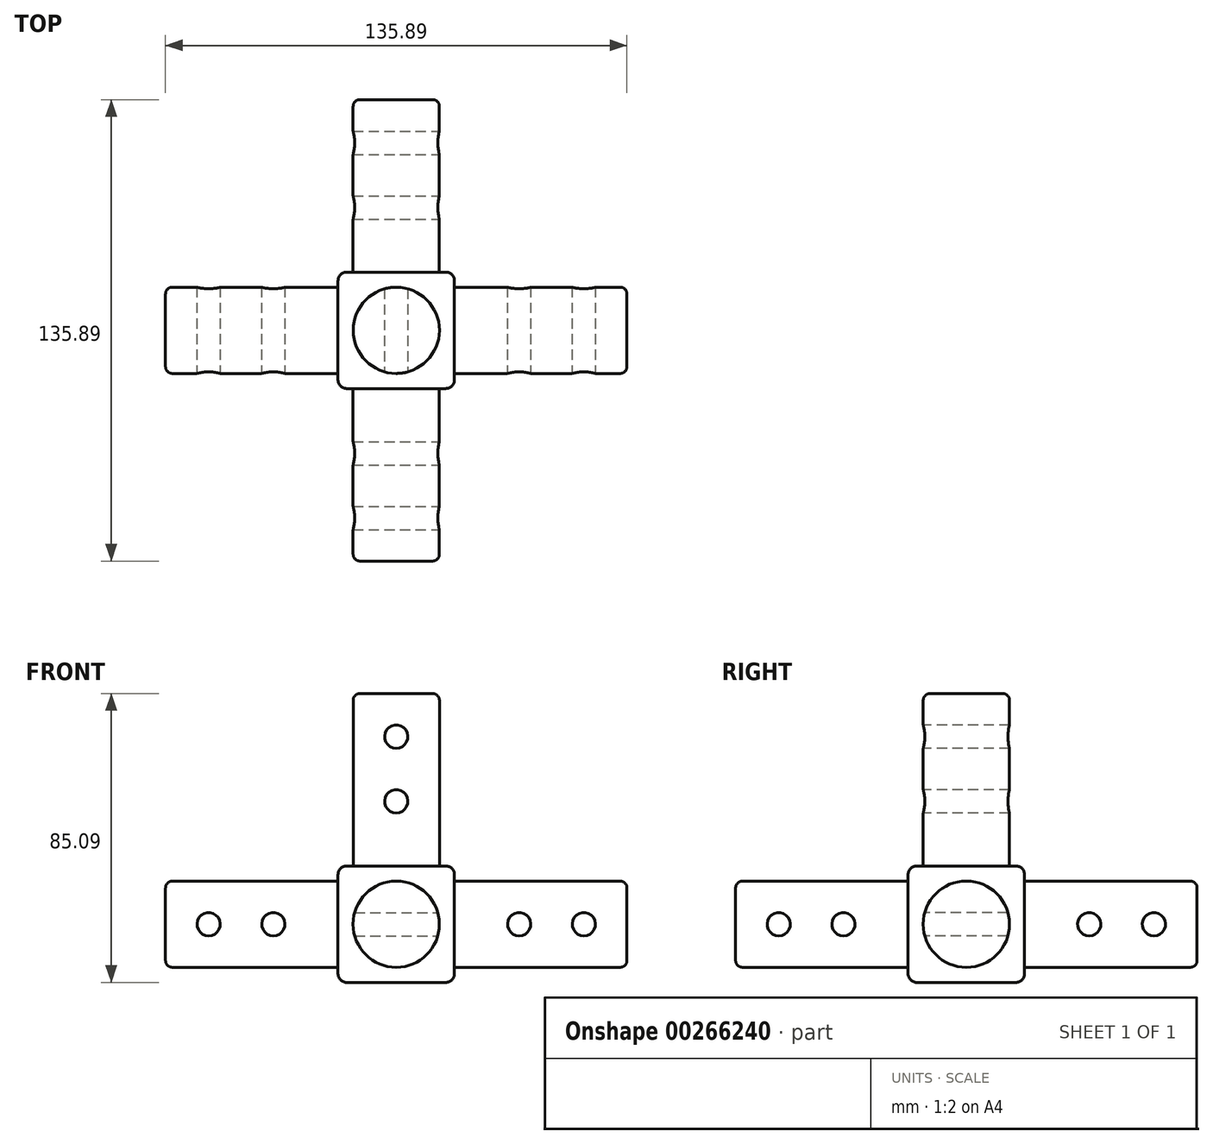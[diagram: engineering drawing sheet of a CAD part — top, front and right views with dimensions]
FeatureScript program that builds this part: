
annotation { "Feature Type Name" : "Feature", "Feature Type Description" : "" }
export const myFeature = defineFeature(function(context is Context, id is Id, definition is map)
    precondition{}
    {
        {
            var Q0;
            Q0=qCreatedBy(makeId("Top.planeOp"),FACE);
            var sketch = newSketch(context, id + "F0", { "sketchPlane" : qUnion([Q0])});
            skLineSegment(sketch, "E0.bottom", {"start": v(-13.47, 23.7) * mm, "end": v(20.82, 23.7) * mm});
            skLineSegment(sketch, "E0.top", {"start": v(-13.47, -10.58) * mm, "end": v(20.82, -10.58) * mm});
            skLineSegment(sketch, "E0.left", {"start": v(-13.47, 23.7) * mm, "end": v(-13.47, -10.58) * mm});
            skLineSegment(sketch, "E0.right", {"start": v(20.82, 23.7) * mm, "end": v(20.82, -10.58) * mm});
            skSolve(sketch);
        }
        {
            var Q0;
            Q0=qSketchRegion(id+"F0",true);
            extrude(context, id + "F1", {"entities" : qUnion([Q0]), "depth" : 34.3 * mm});
        }
        {
            var Q0;
            Q0=makeQuery(id+"F1.opExtrude","CAP_FACE",FACE,{"disambiguationData":[OSD([sQuery(id+"F0.wireOp",EDGE,"E0.bottom"),sQuery(id+"F0.wireOp",EDGE,"E0.top"),sQuery(id+"F0.wireOp",EDGE,"E0.left"),sQuery(id+"F0.wireOp",EDGE,"E0.right")])],"isStart":false});
            var sketch = newSketch(context, id + "F2", { "sketchPlane" : qUnion([Q0])});
            skCircle(sketch, "E1", {"center": v(3.68, 6.56) * mm, "radius": 12.7 * mm});
            skLineSegment(sketch, "E2", {"start": v(3.67, 23.7) * mm, "end": v(3.67, -12.79) * mm, "construction": true});
            skLineSegment(sketch, "E3", {"start": v(20.82, 6.56) * mm, "end": v(-13.47, 6.56) * mm, "construction": true});
            skSolve(sketch);
        }
        {
            var Q0;
            Q0=qSketchRegion(id+"F2",true);
            extrude(context, id + "F3", {"entities" : qUnion([Q0]), "operationType" : NewBodyOperationType.ADD, "depth" : 50.8 * mm});
        }
        {
            var Q0;
            Q0=makeQuery(id+"F1.opExtrude","SWEPT_FACE",FACE,{"disambiguationData":[OSD([sQuery(id+"F0.wireOp",EDGE,"E0.left")])]});
            var sketch = newSketch(context, id + "F4", { "sketchPlane" : qUnion([Q0])});
            skLineSegment(sketch, "E4", {"start": v(-23.7, 17.15) * mm, "end": v(13.45, 17.15) * mm, "construction": true});
            skLineSegment(sketch, "E5", {"start": v(-6.56, 0) * mm, "end": v(-6.56, 34.3) * mm, "construction": true});
            skCircle(sketch, "E6", {"center": v(-6.56, 17.15) * mm, "radius": 12.7 * mm});
            skSolve(sketch);
        }
        {
            var Q0;
            Q0=qSketchRegion(id+"F4",true);
            extrude(context, id + "F5", {"entities" : qUnion([Q0]), "operationType" : NewBodyOperationType.ADD, "depth" : 50.8 * mm});
        }
        {
            var Q0;
            Q0=makeQuery(id+"F1.opExtrude","SWEPT_FACE",FACE,{"disambiguationData":[OSD([sQuery(id+"F0.wireOp",EDGE,"E0.top")])]});
            var sketch = newSketch(context, id + "F6", { "sketchPlane" : qUnion([Q0])});
            skLineSegment(sketch, "E7", {"start": v(-13.47, 17.15) * mm, "end": v(24.43, 17.15) * mm, "construction": true});
            skLineSegment(sketch, "E8", {"start": v(3.67, 0) * mm, "end": v(3.67, 34.3) * mm, "construction": true});
            skCircle(sketch, "E9", {"center": v(3.67, 17.15) * mm, "radius": 12.7 * mm});
            skSolve(sketch);
        }
        {
            var Q0;
            Q0=qSketchRegion(id+"F6",true);
            extrude(context, id + "F7", {"entities" : qUnion([Q0]), "operationType" : NewBodyOperationType.ADD, "depth" : 50.8 * mm});
        }
        {
            var Q0;
            Q0=qCreatedBy(makeId("Front.planeOp"),FACE);
            var sketch = newSketch(context, id + "F8", { "sketchPlane" : qUnion([Q0])});
            skCircle(sketch, "E10", {"center": v(3.67, 53.34) * mm, "radius": 3.43 * mm});
            skCircle(sketch, "E11", {"center": v(3.67, 72.4) * mm, "radius": 3.43 * mm});
            skSolve(sketch);
        }
        {
            var Q0;
            Q0=qSketchRegion(id+"F8",true);
            extrude(context, id + "F9", {"entities" : qUnion([Q0]), "operationType" : NewBodyOperationType.REMOVE, "endBound" : BoundingType.SYMMETRIC, "oppositeDirection" : true, "depth" : 50.8 * mm});
        }
        {
            var Q0;
            Q0=qCreatedBy(makeId("Right.planeOp"),FACE);
            var sketch = newSketch(context, id + "F10", { "sketchPlane" : qUnion([Q0])});
            skCircle(sketch, "E12", {"center": v(-29.63, 17.15) * mm, "radius": 3.43 * mm});
            skCircle(sketch, "E13", {"center": v(-48.68, 17.15) * mm, "radius": 3.43 * mm});
            skSolve(sketch);
        }
        {
            var Q0;
            Q0=qSketchRegion(id+"F10",true);
            extrude(context, id + "F11", {"entities" : qUnion([Q0]), "operationType" : NewBodyOperationType.REMOVE, "endBound" : BoundingType.SYMMETRIC, "oppositeDirection" : true, "depth" : 50.8 * mm});
        }
        {
            var Q0;
            Q0=qCreatedBy(makeId("Front.planeOp"),FACE);
            var sketch = newSketch(context, id + "F12", { "sketchPlane" : qUnion([Q0])});
            skCircle(sketch, "E14", {"center": v(-51.57, 17.15) * mm, "radius": 3.43 * mm});
            skCircle(sketch, "E15", {"center": v(-32.52, 17.15) * mm, "radius": 3.43 * mm});
            skSolve(sketch);
        }
        {
            var Q0;
            Q0=qSketchRegion(id+"F12",true);
            extrude(context, id + "F13", {"entities" : qUnion([Q0]), "operationType" : NewBodyOperationType.REMOVE, "endBound" : BoundingType.SYMMETRIC, "oppositeDirection" : true, "depth" : 50.8 * mm});
        }
        {
            var Q0;
            Q0=makeQuery(id+"F1.opExtrude","SWEPT_EDGE",EDGE,{"disambiguationData":[OSD([sQuery(id+"F0.wireOp",EDGE,"E0.bottom"),sQuery(id+"F0.wireOp",EDGE,"E0.right")])]});
            var Q1;
            Q1=makeQuery(id+"F1.opExtrude","CAP_EDGE",EDGE,{"disambiguationData":[OSD([sQuery(id+"F0.wireOp",EDGE,"E0.right")])],"isStart":false});
            var Q2;
            Q2=makeQuery(id+"F1.opExtrude","SWEPT_EDGE",EDGE,{"disambiguationData":[OSD([sQuery(id+"F0.wireOp",EDGE,"E0.top"),sQuery(id+"F0.wireOp",EDGE,"E0.right")])]});
            var Q3;
            Q3=makeQuery(id+"F1.opExtrude","CAP_EDGE",EDGE,{"disambiguationData":[OSD([sQuery(id+"F0.wireOp",EDGE,"E0.right")])],"isStart":true});
            var Q4;
            Q4=makeQuery(id+"F1.opExtrude","CAP_EDGE",EDGE,{"disambiguationData":[OSD([sQuery(id+"F0.wireOp",EDGE,"E0.bottom")])],"isStart":true});
            var Q5;
            Q5=makeQuery(id+"F1.opExtrude","CAP_EDGE",EDGE,{"disambiguationData":[OSD([sQuery(id+"F0.wireOp",EDGE,"E0.bottom")])],"isStart":false});
            var Q6;
            Q6=makeQuery(id+"F1.opExtrude","SWEPT_EDGE",EDGE,{"disambiguationData":[OSD([sQuery(id+"F0.wireOp",EDGE,"E0.bottom"),sQuery(id+"F0.wireOp",EDGE,"E0.left")])]});
            var Q7;
            Q7=makeQuery(id+"F1.opExtrude","CAP_EDGE",EDGE,{"disambiguationData":[OSD([sQuery(id+"F0.wireOp",EDGE,"E0.left")])],"isStart":true});
            var Q8;
            Q8=makeQuery(id+"F1.opExtrude","CAP_EDGE",EDGE,{"disambiguationData":[OSD([sQuery(id+"F0.wireOp",EDGE,"E0.top")])],"isStart":true});
            var Q9;
            Q9=makeQuery(id+"F1.opExtrude","CAP_EDGE",EDGE,{"disambiguationData":[OSD([sQuery(id+"F0.wireOp",EDGE,"E0.left")])],"isStart":false});
            var Q10;
            Q10=makeQuery(id+"F1.opExtrude","SWEPT_EDGE",EDGE,{"disambiguationData":[OSD([sQuery(id+"F0.wireOp",EDGE,"E0.top"),sQuery(id+"F0.wireOp",EDGE,"E0.left")])]});
            var Q11;
            Q11=makeQuery(id+"F1.opExtrude","CAP_EDGE",EDGE,{"disambiguationData":[OSD([sQuery(id+"F0.wireOp",EDGE,"E0.top")])],"isStart":false});
            fillet(context, id + "F14", {"entities" : qUnion([Q0, Q1, Q2, Q3, Q4, Q5, Q6, Q7, Q8, Q9, Q10, Q11]), "radius" : 2.54 * mm, "tangentPropagation" : true, "allowEdgeOverflow" : false});
        }
        {
            var Q0;
            Q0=makeQuery(id+"F1.opExtrude","SWEPT_FACE",FACE,{"disambiguationData":[OSD([sQuery(id+"F0.wireOp",EDGE,"E0.bottom")])]});
            var sketch = newSketch(context, id + "F15", { "sketchPlane" : qUnion([Q0])});
            skLineSegment(sketch, "E16", {"start": v(-18.28, 17.15) * mm, "end": v(4.82, 17.15) * mm, "construction": true});
            skPoint(sketch, "E16.endSnap0", {"position": v(-18.28, 17.15) * mm});
            skLineSegment(sketch, "E17", {"start": v(-3.67, 31.75) * mm, "end": v(-3.67, 14.65) * mm, "construction": true});
            skCircle(sketch, "E18", {"center": v(-3.67, 17.15) * mm, "radius": 12.7 * mm});
            skSolve(sketch);
        }
        {
            var Q0;
            Q0=qSketchRegion(id+"F15",true);
            extrude(context, id + "F16", {"entities" : qUnion([Q0]), "operationType" : NewBodyOperationType.ADD, "depth" : 50.8 * mm});
        }
        {
            var Q0;
            Q0=qCreatedBy(makeId("Right.planeOp"),FACE);
            var sketch = newSketch(context, id + "F17", { "sketchPlane" : qUnion([Q0])});
            skCircle(sketch, "E19", {"center": v(42.76, 17.15) * mm, "radius": 3.43 * mm});
            skCircle(sketch, "E20", {"center": v(61.8, 17.15) * mm, "radius": 3.43 * mm});
            skSolve(sketch);
        }
        {
            var Q0;
            Q0=qSketchRegion(id+"F17",true);
            extrude(context, id + "F18", {"entities" : qUnion([Q0]), "operationType" : NewBodyOperationType.REMOVE, "endBound" : BoundingType.SYMMETRIC, "oppositeDirection" : true, "depth" : 50.8 * mm});
        }
        {
            var Q0;
            Q0=makeQuery(id+"F1.opExtrude","SWEPT_FACE",FACE,{"disambiguationData":[OSD([sQuery(id+"F0.wireOp",EDGE,"E0.right")])]});
            var sketch = newSketch(context, id + "F19", { "sketchPlane" : qUnion([Q0])});
            skCircle(sketch, "E21", {"center": v(6.56, 17.14) * mm, "radius": 12.7 * mm});
            skLineSegment(sketch, "E22", {"start": v(-8.04, 17.15) * mm, "end": v(28.63, 17.15) * mm, "construction": true});
            skLineSegment(sketch, "E23", {"start": v(6.56, 2.54) * mm, "end": v(6.56, 27.82) * mm, "construction": true});
            skSolve(sketch);
        }
        {
            var Q0;
            Q0=qSketchRegion(id+"F19",true);
            extrude(context, id + "F20", {"entities" : qUnion([Q0]), "operationType" : NewBodyOperationType.ADD, "depth" : 50.8 * mm});
        }
        {
            var Q0;
            Q0=makeQuery(id+"F3.opExtrude","CAP_EDGE",EDGE,{"disambiguationData":[OSD([sQuery(id+"F2.wireOp",EDGE,"E1")])],"isStart":false});
            var Q1;
            Q1=makeQuery(id+"F7.opExtrude","CAP_EDGE",EDGE,{"disambiguationData":[OSD([sQuery(id+"F6.wireOp",EDGE,"E9")])],"isStart":false});
            var Q2;
            Q2=makeQuery(id+"F5.opExtrude","CAP_EDGE",EDGE,{"disambiguationData":[OSD([sQuery(id+"F4.wireOp",EDGE,"E6")])],"isStart":false});
            var Q3;
            Q3=makeQuery(id+"F16.opExtrude","CAP_EDGE",EDGE,{"disambiguationData":[OSD([sQuery(id+"F15.wireOp",EDGE,"E18")])],"isStart":false});
            var Q4;
            Q4=makeQuery(id+"F20.opExtrude","CAP_EDGE",EDGE,{"disambiguationData":[OSD([sQuery(id+"F19.wireOp",EDGE,"E21")])],"isStart":false});
            fillet(context, id + "F21", {"entities" : qUnion([Q0, Q1, Q2, Q3, Q4]), "radius" : 2.03 * mm, "tangentPropagation" : true, "allowEdgeOverflow" : false});
        }
        {
            var Q0;
            Q0=qCreatedBy(makeId("Front.planeOp"),FACE);
            var sketch = newSketch(context, id + "F22", { "sketchPlane" : qUnion([Q0])});
            skCircle(sketch, "E24", {"center": v(58.92, 17.15) * mm, "radius": 3.43 * mm});
            skCircle(sketch, "E25", {"center": v(39.87, 17.15) * mm, "radius": 3.43 * mm});
            skSolve(sketch);
        }
        {
            var Q0;
            Q0=qSketchRegion(id+"F22",true);
            extrude(context, id + "F23", {"entities" : qUnion([Q0]), "operationType" : NewBodyOperationType.REMOVE, "endBound" : BoundingType.SYMMETRIC, "oppositeDirection" : true, "depth" : 50.8 * mm});
        }
    });
